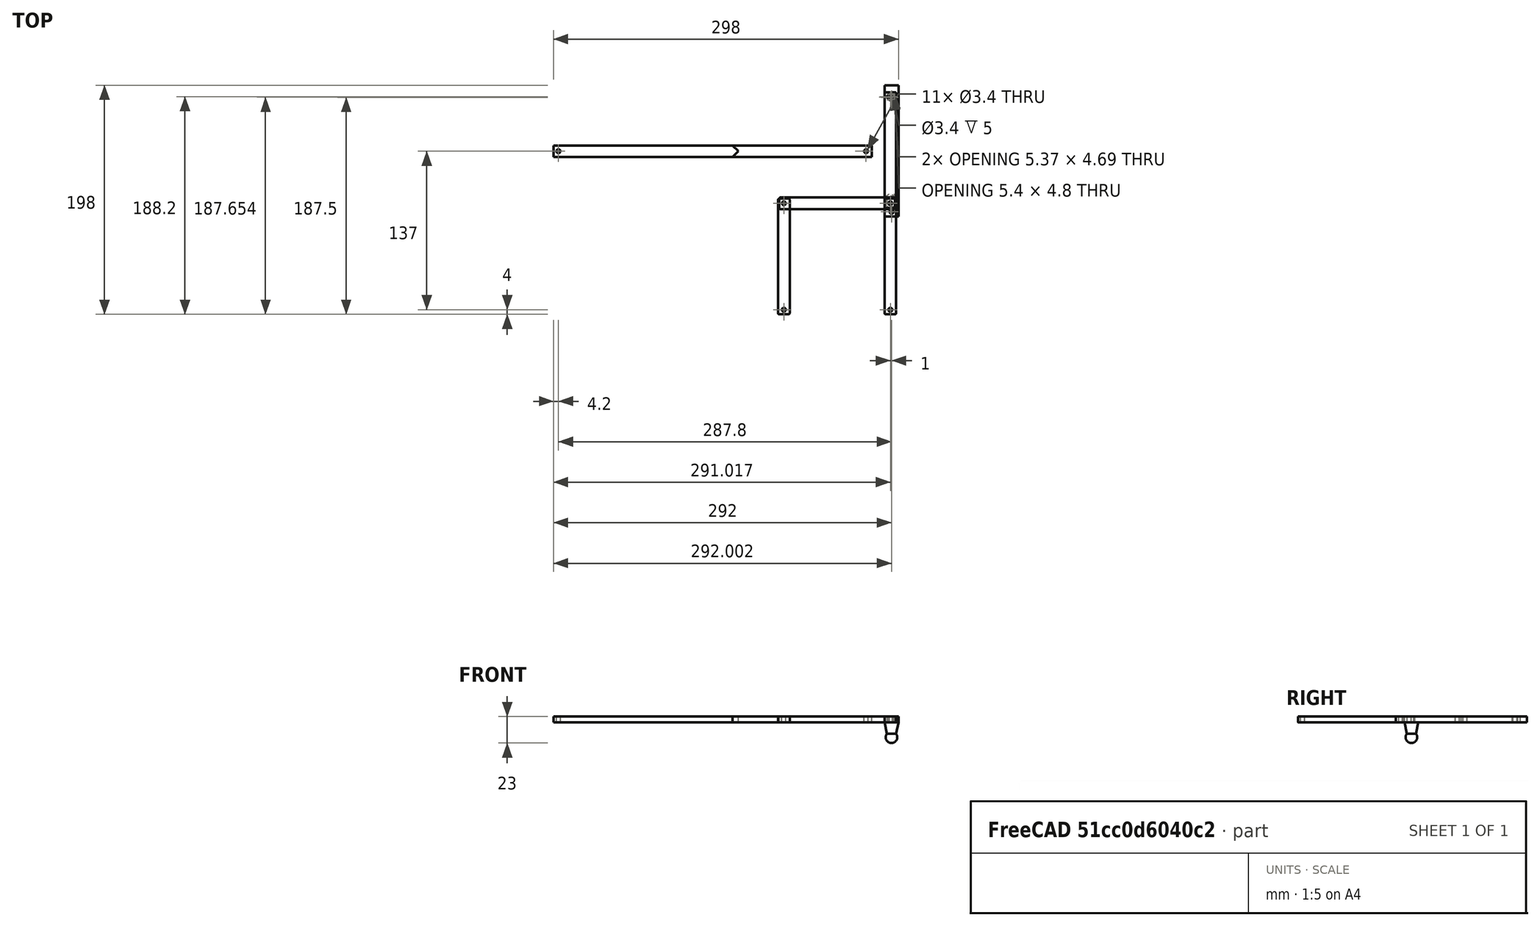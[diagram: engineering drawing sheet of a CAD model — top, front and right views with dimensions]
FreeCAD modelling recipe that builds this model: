
FCSTD DOCUMENT  (FreeCAD 0.14R3702 (Git))
Label: handdrivensquare
License: CC-BY 3.0
LicenseURL: http://creativecommons.org/licenses/by/3.0/
objects: Part::Fillet×12, Part::Cut×11, Part::Box×9, Part::Cylinder×8, Part::Fuse×4, Part::MultiCommon×1, Part::Cone×1, Part::Sphere×1
note: 47 computed .brp shape members not serialized (recipe doc carries the construction recipe); baked Part::Feature solids carry a one-line shape summary decoded from their .brp

FEATURE [Part::Box] Box  label="Cube"
  Height = 5
  Length = 100
  Width = 10
FEATURE [Part::Cylinder] Cylinder
  Angle = 360
  Height = 10
  Placement = pos=(4,5,-1) rot=(0,0,1;0rad)
  Radius = 1.7
FEATURE [Part::Cylinder] Cylinder001
  Angle = 360
  Height = 10
  Placement = pos=(96,5,-2) rot=(0,0,1;0rad)
  Radius = 1.7
FEATURE [Part::Cut] Cut
  Base = -> Box
  Tool = -> Cylinder
FEATURE [Part::Cut] Cut001
  Base = -> Cut
  Tool = -> Cylinder001
FEATURE [Part::Fillet] Fillet
  Base = -> Cut001
  Edges = 1 edges r=1: [Edge13]
FEATURE [Part::Fillet] Fillet001
  Base = -> Fillet
  Edges = 1 edges r=1: [Edge15]
FEATURE [Part::Fillet] Fillet002
  Base = -> Fillet001
  Edges = 1 edges r=1: [Edge17]
FEATURE [Part::Fillet] Fillet003
  Base = -> Fillet002
  Edges = 1 edges r=1: [Edge17]
FEATURE [Part::Fillet] Fillet005
  Base = -> Fillet001
  Edges = 1 edges r=1: [Edge17]
FEATURE [Part::Fillet] Fillet004
  Base = -> Fillet005
  Edges = 1 edges r=1: [Edge17]
  Placement = pos=(-1,9,0) rot=(0,0,-1;1.5708rad)
FEATURE [Part::Fillet] Fillet007
  Base = -> Fillet001
  Edges = 1 edges r=1: [Edge17]
FEATURE [Part::Fillet] Fillet006
  Base = -> Fillet007
  Edges = 1 edges r=1: [Edge17]
  Placement = pos=(101,-91,0) rot=(0,0,1;1.5708rad)
FEATURE [Part::Fillet] Fillet009
  Base = -> Fillet001
  Edges = 1 edges r=1: [Edge17]
FEATURE [Part::Fillet] Fillet008
  Base = -> Fillet009
  Edges = 1 edges r=1: [Edge17]
  Placement = pos=(101,1,0) rot=(0,0,1;1.5708rad)
FEATURE [Part::Cylinder] Cylinder002
  Angle = 360
  Height = 10
  Placement = pos=(96,97,-3) rot=(0,0,1;0rad)
  Radius = 2.7
FEATURE [Part::Box] Box001  label="Cube001"
  Height = 10
  Length = 10
  Placement = pos=(90.8,99,-3) rot=(0,0,1;0rad)
  Width = 10
FEATURE [Part::Cut] Cut002
  Base = -> Cylinder002
  Tool = -> Box001
FEATURE [Part::Cut] Cut003
  Base = -> Fillet008
  Tool = -> Cut002
FEATURE [Part::Fillet] Fillet011
  Base = -> Fillet001
  Edges = 1 edges r=1: [Edge17]
FEATURE [Part::Fillet] Fillet010
  Base = -> Fillet011
  Edges = 1 edges r=1: [Edge17]
  Placement = pos=(-1,9,0) rot=(0,0,-1;1.5708rad)
FEATURE [Part::Box] Box002  label="Cube002"
  Height = 5
  Length = 275
  Placement = pos=(-195,45,0) rot=(0,0,1;0rad)
  Width = 10
FEATURE [Part::Cylinder] Cylinder003
  Angle = 360
  Height = 10
  Placement = pos=(-190.8,50,-2) rot=(0,0,1;0rad)
  Radius = 1.7
FEATURE [Part::Cylinder] Cylinder004
  Angle = 360
  Height = 10
  Placement = pos=(75,50,-2) rot=(0,0,1;0rad)
  Radius = 1.7
FEATURE [Part::Box] Box003  label="Cube003"
  Height = 10
  Length = 400
  Placement = pos=(-601,50,-3) rot=(0,0,-1;0.785398rad)
  Width = 400
FEATURE [Part::Box] Box004  label="Cube004"
  Height = 5
  Length = 275
  Placement = pos=(-195,45,0) rot=(0,0,1;0rad)
  Width = 10
FEATURE [Part::Cut] Cut004
  Base = -> Box004
  Tool = -> Box003
FEATURE [Part::Box] Box005  label="Cube005"
  Height = 10
  Length = 400
  Placement = pos=(-601,50,-3) rot=(0,0,-1;0.785398rad)
  Width = 400
FEATURE [Part::MultiCommon] Common
  Shapes = -> [Box002,Box005]
FEATURE [Part::Cut] Cut005  label="Long arm part a"
  Base = -> Cut004
  Tool = -> Cylinder004
FEATURE [Part::Cut] Cut006  label="long arm part b"
  Base = -> Common
  Tool = -> Cylinder003
FEATURE [Part::Box] Box006  label="Cube006"
  Height = 5
  Length = 12
  Placement = pos=(91,-5,0) rot=(0,0,1;0rad)
  Width = 113.4
FEATURE [Part::Cylinder] Cylinder005
  Angle = 360
  Height = 10
  Placement = pos=(97,97,-3) rot=(0,0,1;0rad)
  Radius = 2.7
FEATURE [Part::Box] Box007  label="Cube007"
  Height = 10
  Length = 10
  Placement = pos=(91.8,99,-3) rot=(0,0,1;0rad)
  Width = 10
FEATURE [Part::Cut] Cut007
  Base = -> Cylinder005
  Placement = pos=(0,2,0) rot=(0,0,1;0rad)
  Tool = -> Box007
FEATURE [Part::Cut] Cut008
  Base = -> Box006
  Placement = pos=(0,-1.4,0) rot=(0,0,1;0rad)
  Tool = -> Cut007
FEATURE [Part::Cylinder] Cylinder006
  Angle = 360
  Height = 10
  Placement = pos=(97,-2.4,-1) rot=(0,0,1;0rad)
  Radius = 1.7
FEATURE [Part::Cut] Cut009
  Base = -> Cut008
  Tool = -> Cylinder006
FEATURE [Part::Cone] Cone
  Angle = 360
  Height = 10
  Placement = pos=(97,7,-10) rot=(0,0,1;0rad)
  Radius1 = 4
  Radius2 = 6
FEATURE [Part::Sphere] Sphere
  Angle1 = -90
  Angle2 = 90
  Angle3 = 360
  Placement = pos=(97,7,-13) rot=(0,0,1;0rad)
  Radius = 5
FEATURE [Part::Fuse] Fusion
  Base = -> Cut009
  Tool = -> Cone
FEATURE [Part::Fuse] Fusion001
  Base = -> Sphere
  Tool = -> Fusion
FEATURE [Part::Box] Box008  label="Cube008"
  Height = 5
  Length = 12
  Placement = pos=(91,92,0) rot=(0,0,1;0rad)
  Width = 10
FEATURE [Part::Fuse] Fusion002
  Base = -> Fusion001
  Tool = -> Box008
FEATURE [Part::Fuse] Fusion003
  Base = -> Fusion001
  Tool = -> Box008
FEATURE [Part::Cylinder] Cylinder007
  Angle = 360
  Height = 10
  Placement = pos=(97,96.5,0) rot=(0,0,1;0rad)
  Radius = 1.7
FEATURE [Part::Cut] Cut010
  Base = -> Fusion003
  Tool = -> Cylinder007
